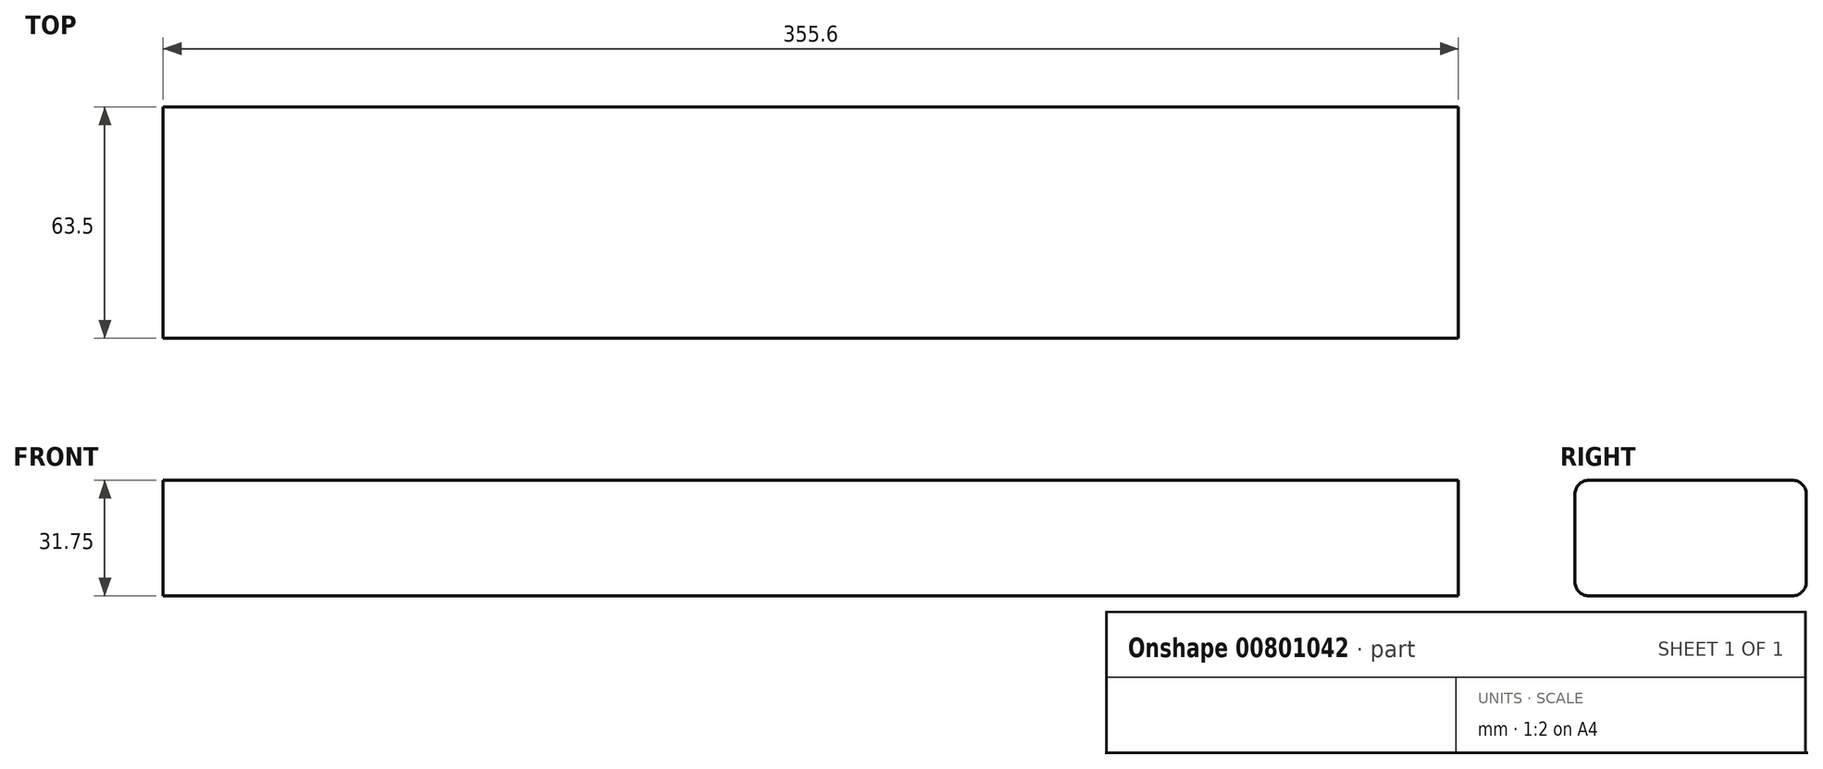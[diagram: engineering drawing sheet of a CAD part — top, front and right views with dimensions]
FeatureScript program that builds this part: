
annotation { "Feature Type Name" : "Feature", "Feature Type Description" : "" }
export const myFeature = defineFeature(function(context is Context, id is Id, definition is map)
    precondition{}
    {
        {
            var Q0;
            Q0=qCreatedBy(makeId("Top.planeOp"),FACE);
            var sketch = newSketch(context, id + "F0", { "sketchPlane" : qUnion([Q0])});
            skLineSegment(sketch, "E0.bottom", {"start": v(0, 0) * mm, "end": v(355.6, 0) * mm});
            skLineSegment(sketch, "E0.top", {"start": v(0, 63.5) * mm, "end": v(355.6, 63.5) * mm});
            skLineSegment(sketch, "E0.left", {"start": v(0, 0) * mm, "end": v(0, 63.5) * mm});
            skLineSegment(sketch, "E0.right", {"start": v(355.6, 0) * mm, "end": v(355.6, 63.5) * mm});
            skSolve(sketch);
        }
        {
            var Q0;
            Q0=makeQuery(id+"F0.imprint","IMPRINT",FACE,{"disambiguationData":[TD([[makeQuery(id+"F0.imprint","IMPRINT",EDGE,{"derivedFrom":sQuery(id+"F0.wireOp",EDGE,"E0.bottom")}),1.0]])]});
            extrude(context, id + "F1", {"entities" : qUnion([Q0]), "depth" : 31.75 * mm, "offsetDistance" : 25.4 * mm});
        }
        {
            var Q0;
            Q0=makeQuery(id+"F1.opExtrude","CAP_EDGE",EDGE,{"disambiguationData":[OSD([sQuery(id+"F0.wireOp",EDGE,"E0.bottom")])],"isStart":false});
            var Q1;
            Q1=makeQuery(id+"F1.opExtrude","CAP_EDGE",EDGE,{"disambiguationData":[OSD([sQuery(id+"F0.wireOp",EDGE,"E0.bottom")])],"isStart":true});
            var Q2;
            Q2=makeQuery(id+"F1.opExtrude","CAP_EDGE",EDGE,{"disambiguationData":[OSD([sQuery(id+"F0.wireOp",EDGE,"E0.top")])],"isStart":false});
            var Q3;
            Q3=makeQuery(id+"F1.opExtrude","CAP_EDGE",EDGE,{"disambiguationData":[OSD([sQuery(id+"F0.wireOp",EDGE,"E0.top")])],"isStart":true});
            fillet(context, id + "F2", {"entities" : qUnion([Q0, Q1, Q2, Q3]), "radius" : 3.8 * mm, "tangentPropagation" : true, "allowEdgeOverflow" : false});
        }
    });
